FREECAD ASSEMBLY — COMPONENT RECIPES ("#110-000 Assembly3")

This assembly document has 90 components, labeled P0..P89 below (a component is one placed body or linked part). 0 of them carry a construction recipe — the FreeCAD feature program that regenerates the part from scratch, quoted from this document or its linked companion documents; the rest are supplied as boundary geometry only. No exploded tour is included for this assembly.
COMPONENT P0 — geometry summary ("XR5_R_CC25_P10.16_H_5DD3C33E001"; no construction recipe available for this part):
  bounding box: 10.7 x 5.1 x 2.5 mm
  tessellated surface: 5,540 triangles
  volume: 34 mm^3 (25% of its bounding box)
  symmetry: 2-fold rotationally symmetric about the z axis; mirror-symmetric across its x mid-plane, y mid-plane
COMPONENT P1 — geometry summary ("RV55_Alpha_RV16AF-41-15R-XXX_5DD3C758"; no construction recipe available for this part):
  bounding box: 30.7 x 24.7 x 17.0 mm
  tessellated surface: 23,788 triangles
  volume: 1291 mm^3 (10% of its bounding box)
COMPONENT P2 — geometry summary ("JP20_R_0R_Wire_Jumper_P10.16_5DC277DA001"; no construction recipe available for this part):
  bounding box: 10.7 x 3.6 x 0.6 mm
  tessellated surface: 2,588 triangles
  volume: 4 mm^3 (18% of its bounding box)
  symmetry: 2-fold rotationally symmetric about the z axis; mirror-symmetric across its x mid-plane, y mid-plane
COMPONENT P3 — geometry summary ("JP20_R_0R_Wire_Jumper_P10.16_5DC277DA002"; no construction recipe available for this part):
  bounding box: 10.7 x 3.6 x 0.6 mm
  tessellated surface: 2,588 triangles
  volume: 4 mm^3 (18% of its bounding box)
  symmetry: 2-fold rotationally symmetric about the z axis; mirror-symmetric across its x mid-plane, y mid-plane
COMPONENT P4 — geometry summary ("JP20_R_0R_Wire_Jumper_P10.16_5DC277DA003"; no construction recipe available for this part):
  bounding box: 10.7 x 3.6 x 0.6 mm
  tessellated surface: 2,588 triangles
  volume: 4 mm^3 (18% of its bounding box)
  symmetry: 2-fold rotationally symmetric about the z axis; mirror-symmetric across its x mid-plane, y mid-plane
COMPONENT P5 — geometry summary ("JP20_R_0R_Wire_Jumper_P10.16_5DC277DA004"; no construction recipe available for this part):
  bounding box: 10.7 x 3.6 x 0.6 mm
  tessellated surface: 2,588 triangles
  volume: 4 mm^3 (18% of its bounding box)
  symmetry: 2-fold rotationally symmetric about the z axis; mirror-symmetric across its x mid-plane, y mid-plane
COMPONENT P6 — geometry summary ("JP20_R_0R_Wire_Jumper_P10.16_5DC277DA005"; no construction recipe available for this part):
  bounding box: 10.7 x 3.6 x 0.6 mm
  tessellated surface: 2,588 triangles
  volume: 4 mm^3 (18% of its bounding box)
  symmetry: 2-fold rotationally symmetric about the z axis; mirror-symmetric across its x mid-plane, y mid-plane
COMPONENT P7 — geometry summary ("JP20_R_0R_Wire_Jumper_P10.16_5DC277DA006"; no construction recipe available for this part):
  bounding box: 10.7 x 3.6 x 0.6 mm
  tessellated surface: 2,588 triangles
  volume: 4 mm^3 (18% of its bounding box)
  symmetry: 2-fold rotationally symmetric about the z axis; mirror-symmetric across its x mid-plane, y mid-plane
COMPONENT P8 — geometry summary ("JP20_R_0R_Wire_Jumper_P10.16_5DC277DA007"; no construction recipe available for this part):
  bounding box: 10.7 x 3.6 x 0.6 mm
  tessellated surface: 2,588 triangles
  volume: 4 mm^3 (18% of its bounding box)
  symmetry: 2-fold rotationally symmetric about the z axis; mirror-symmetric across its x mid-plane, y mid-plane
COMPONENT P9 — geometry summary ("JP20_R_0R_Wire_Jumper_P10.16_5DC277DA008"; no construction recipe available for this part):
  bounding box: 10.7 x 3.6 x 0.6 mm
  tessellated surface: 2,588 triangles
  volume: 4 mm^3 (18% of its bounding box)
  symmetry: 2-fold rotationally symmetric about the z axis; mirror-symmetric across its x mid-plane, y mid-plane
COMPONENT P10 — geometry summary ("JP20_R_0R_Wire_Jumper_P10.16_5DC277DA009"; no construction recipe available for this part):
  bounding box: 10.7 x 3.6 x 0.6 mm
  tessellated surface: 2,588 triangles
  volume: 4 mm^3 (18% of its bounding box)
  symmetry: 2-fold rotationally symmetric about the z axis; mirror-symmetric across its x mid-plane, y mid-plane
COMPONENT P11 — geometry summary ("JP20_R_0R_Wire_Jumper_P10.16_5DC277DA010"; no construction recipe available for this part):
  bounding box: 10.7 x 3.6 x 0.6 mm
  tessellated surface: 2,588 triangles
  volume: 4 mm^3 (18% of its bounding box)
  symmetry: 2-fold rotationally symmetric about the z axis; mirror-symmetric across its x mid-plane, y mid-plane
COMPONENT P12 — geometry summary ("JP20_R_0R_Wire_Jumper_P10.16_5DC277DA011"; no construction recipe available for this part):
  bounding box: 10.7 x 3.6 x 0.6 mm
  tessellated surface: 2,588 triangles
  volume: 4 mm^3 (18% of its bounding box)
  symmetry: 2-fold rotationally symmetric about the z axis; mirror-symmetric across its x mid-plane, y mid-plane
COMPONENT P13 — geometry summary ("JP20_R_0R_Wire_Jumper_P10.16_5DC277DA012"; no construction recipe available for this part):
  bounding box: 10.7 x 3.6 x 0.6 mm
  tessellated surface: 2,588 triangles
  volume: 4 mm^3 (18% of its bounding box)
  symmetry: 2-fold rotationally symmetric about the z axis; mirror-symmetric across its x mid-plane, y mid-plane
COMPONENT P14 — geometry summary ("JP20_R_0R_Wire_Jumper_P10.16_5DC277DA013"; no construction recipe available for this part):
  bounding box: 10.7 x 3.6 x 0.6 mm
  tessellated surface: 2,588 triangles
  volume: 4 mm^3 (18% of its bounding box)
  symmetry: 2-fold rotationally symmetric about the z axis; mirror-symmetric across its x mid-plane, y mid-plane
COMPONENT P15 — geometry summary ("JP20_R_0R_Wire_Jumper_P10.16_5DC277DA014"; no construction recipe available for this part):
  bounding box: 10.7 x 3.6 x 0.6 mm
  tessellated surface: 2,588 triangles
  volume: 4 mm^3 (18% of its bounding box)
  symmetry: 2-fold rotationally symmetric about the z axis; mirror-symmetric across its x mid-plane, y mid-plane
COMPONENT P16 — geometry summary ("XC10_Nichicon_UMA_Straight_D5_H5_P2_d0.45_LL2.6_5DC00C0A001"; no construction recipe available for this part):
  bounding box: 7.6 x 5.0 x 5.0 mm
  tessellated surface: 17,406 triangles
  volume: 97 mm^3 (51% of its bounding box)
  symmetry: 2-fold rotationally symmetric about the z axis; mirror-symmetric across its x mid-plane, y mid-plane
COMPONENT P17 — geometry summary ("XC12_Nichicon_UMA_Straight_D8_H5_P2.5_d0.45_LL2.6_5DCF4B088"; no construction recipe available for this part):
  bounding box: 8.0 x 8.0 x 7.6 mm
  tessellated surface: 17,380 triangles
  volume: 248 mm^3 (51% of its bounding box)
  symmetry: 2-fold rotationally symmetric about the z axis; mirror-symmetric across its x mid-plane, y mid-plane
COMPONENT P18 — geometry summary ("XC10_Nichicon_UMA_Straight_D5_H5_P2_d0.45_LL2.6_5DC00C0A002"; no construction recipe available for this part):
  bounding box: 7.6 x 5.0 x 5.0 mm
  tessellated surface: 17,406 triangles
  volume: 97 mm^3 (51% of its bounding box)
  symmetry: 2-fold rotationally symmetric about the z axis; mirror-symmetric across its x mid-plane, y mid-plane
COMPONENT P19 — geometry summary ("XD6_DO-41_P10.16_5DC00C073"; no construction recipe available for this part):
  bounding box: 10.9 x 5.0 x 2.4 mm
  tessellated surface: 7,540 triangles
  volume: 26 mm^3 (20% of its bounding box)
  symmetry: 2-fold rotationally symmetric about the z axis
COMPONENT P20 — geometry summary ("XD6_DO-41_P10.16_5DC00C074"; no construction recipe available for this part):
  bounding box: 10.9 x 5.0 x 2.4 mm
  tessellated surface: 7,540 triangles
  volume: 26 mm^3 (20% of its bounding box)
  symmetry: 2-fold rotationally symmetric about the z axis
COMPONENT P21 — geometry summary ("XR5_R_CC25_P10.16_H_5DD3C33E002"; no construction recipe available for this part):
  bounding box: 10.7 x 5.1 x 2.5 mm
  tessellated surface: 5,540 triangles
  volume: 34 mm^3 (25% of its bounding box)
  symmetry: 2-fold rotationally symmetric about the z axis; mirror-symmetric across its x mid-plane, y mid-plane
COMPONENT P22 — geometry summary ("XR5_R_CC25_P10.16_H_5DD3C33E003"; no construction recipe available for this part):
  bounding box: 10.7 x 5.1 x 2.5 mm
  tessellated surface: 5,540 triangles
  volume: 34 mm^3 (25% of its bounding box)
  symmetry: 2-fold rotationally symmetric about the z axis; mirror-symmetric across its x mid-plane, y mid-plane
COMPONENT P23 — geometry summary ("XR5_R_CC25_P10.16_H_5DD3C33E004"; no construction recipe available for this part):
  bounding box: 10.7 x 5.1 x 2.5 mm
  tessellated surface: 5,540 triangles
  volume: 34 mm^3 (25% of its bounding box)
  symmetry: 2-fold rotationally symmetric about the z axis; mirror-symmetric across its x mid-plane, y mid-plane
COMPONENT P24 — geometry summary ("XR5_R_CC25_P10.16_H_5DD3C33E005"; no construction recipe available for this part):
  bounding box: 10.7 x 5.1 x 2.5 mm
  tessellated surface: 5,540 triangles
  volume: 34 mm^3 (25% of its bounding box)
  symmetry: 2-fold rotationally symmetric about the z axis; mirror-symmetric across its x mid-plane, y mid-plane
COMPONENT P25 — geometry summary ("XR5_R_CC25_P10.16_H_5DD3C33E006"; no construction recipe available for this part):
  bounding box: 10.7 x 5.1 x 2.5 mm
  tessellated surface: 5,540 triangles
  volume: 34 mm^3 (25% of its bounding box)
  symmetry: 2-fold rotationally symmetric about the z axis; mirror-symmetric across its x mid-plane, y mid-plane
COMPONENT P26 — geometry summary ("XR5_R_CC25_P10.16_H_5DD3C33E007"; no construction recipe available for this part):
  bounding box: 10.7 x 5.1 x 2.5 mm
  tessellated surface: 5,540 triangles
  volume: 34 mm^3 (25% of its bounding box)
  symmetry: 2-fold rotationally symmetric about the z axis; mirror-symmetric across its x mid-plane, y mid-plane
COMPONENT P27 — geometry summary ("XR5_R_CC25_P10.16_H_5DD3C33E008"; no construction recipe available for this part):
  bounding box: 10.7 x 5.1 x 2.5 mm
  tessellated surface: 5,540 triangles
  volume: 34 mm^3 (25% of its bounding box)
  symmetry: 2-fold rotationally symmetric about the z axis; mirror-symmetric across its x mid-plane, y mid-plane
COMPONENT P28 — geometry summary ("XR5_R_CC25_P10.16_H_5DD3C33E009"; no construction recipe available for this part):
  bounding box: 10.7 x 5.1 x 2.5 mm
  tessellated surface: 5,540 triangles
  volume: 34 mm^3 (25% of its bounding box)
  symmetry: 2-fold rotationally symmetric about the z axis; mirror-symmetric across its x mid-plane, y mid-plane
COMPONENT P29 — geometry summary ("XR5_R_CC25_P10.16_H_5DD3C33E010"; no construction recipe available for this part):
  bounding box: 10.7 x 5.1 x 2.5 mm
  tessellated surface: 5,540 triangles
  volume: 34 mm^3 (25% of its bounding box)
  symmetry: 2-fold rotationally symmetric about the z axis; mirror-symmetric across its x mid-plane, y mid-plane
COMPONENT P30 — geometry summary ("XR5_R_CC25_P10.16_H_5DD3C33E011"; no construction recipe available for this part):
  bounding box: 10.7 x 5.1 x 2.5 mm
  tessellated surface: 5,540 triangles
  volume: 34 mm^3 (25% of its bounding box)
  symmetry: 2-fold rotationally symmetric about the z axis; mirror-symmetric across its x mid-plane, y mid-plane
COMPONENT P31 — geometry summary ("XR5_R_CC25_P10.16_H_5DD3C33E012"; no construction recipe available for this part):
  bounding box: 10.7 x 5.1 x 2.5 mm
  tessellated surface: 5,540 triangles
  volume: 34 mm^3 (25% of its bounding box)
  symmetry: 2-fold rotationally symmetric about the z axis; mirror-symmetric across its x mid-plane, y mid-plane
COMPONENT P32 — geometry summary ("XR5_R_CC25_P10.16_H_5DD3C33E013"; no construction recipe available for this part):
  bounding box: 10.7 x 5.1 x 2.5 mm
  tessellated surface: 5,540 triangles
  volume: 34 mm^3 (25% of its bounding box)
  symmetry: 2-fold rotationally symmetric about the z axis; mirror-symmetric across its x mid-plane, y mid-plane
COMPONENT P33 — geometry summary ("XR5_R_CC25_P10.16_H_5DD3C33E014"; no construction recipe available for this part):
  bounding box: 10.7 x 5.1 x 2.5 mm
  tessellated surface: 5,540 triangles
  volume: 34 mm^3 (25% of its bounding box)
  symmetry: 2-fold rotationally symmetric about the z axis; mirror-symmetric across its x mid-plane, y mid-plane
COMPONENT P34 — geometry summary ("XR5_R_CC25_P10.16_H_5DD3C33E015"; no construction recipe available for this part):
  bounding box: 10.7 x 5.1 x 2.5 mm
  tessellated surface: 5,540 triangles
  volume: 34 mm^3 (25% of its bounding box)
  symmetry: 2-fold rotationally symmetric about the z axis; mirror-symmetric across its x mid-plane, y mid-plane
COMPONENT P35 — geometry summary ("XR5_R_CC25_P10.16_H_5DD3C33E016"; no construction recipe available for this part):
  bounding box: 10.7 x 5.1 x 2.5 mm
  tessellated surface: 5,540 triangles
  volume: 34 mm^3 (25% of its bounding box)
  symmetry: 2-fold rotationally symmetric about the z axis; mirror-symmetric across its x mid-plane, y mid-plane
COMPONENT P36 — geometry summary ("XR5_R_CC25_P10.16_H_5DD3C33E017"; no construction recipe available for this part):
  bounding box: 10.7 x 5.1 x 2.5 mm
  tessellated surface: 5,540 triangles
  volume: 34 mm^3 (25% of its bounding box)
  symmetry: 2-fold rotationally symmetric about the z axis; mirror-symmetric across its x mid-plane, y mid-plane
COMPONENT P37 — geometry summary ("XR5_R_CC25_P10.16_H_5DD3C33E018"; no construction recipe available for this part):
  bounding box: 10.7 x 5.1 x 2.5 mm
  tessellated surface: 5,540 triangles
  volume: 34 mm^3 (25% of its bounding box)
  symmetry: 2-fold rotationally symmetric about the z axis; mirror-symmetric across its x mid-plane, y mid-plane
COMPONENT P38 — geometry summary ("XR5_R_CC25_P10.16_H_5DD3C33E019"; no construction recipe available for this part):
  bounding box: 10.7 x 5.1 x 2.5 mm
  tessellated surface: 5,540 triangles
  volume: 34 mm^3 (25% of its bounding box)
  symmetry: 2-fold rotationally symmetric about the z axis; mirror-symmetric across its x mid-plane, y mid-plane
COMPONENT P39 — geometry summary ("XR5_R_CC25_P10.16_H_5DD3C33E020"; no construction recipe available for this part):
  bounding box: 10.7 x 5.1 x 2.5 mm
  tessellated surface: 5,540 triangles
  volume: 34 mm^3 (25% of its bounding box)
  symmetry: 2-fold rotationally symmetric about the z axis; mirror-symmetric across its x mid-plane, y mid-plane
COMPONENT P40 — geometry summary ("XR5_R_CC25_P10.16_H_5DD3C33E021"; no construction recipe available for this part):
  bounding box: 10.7 x 5.1 x 2.5 mm
  tessellated surface: 5,540 triangles
  volume: 34 mm^3 (25% of its bounding box)
  symmetry: 2-fold rotationally symmetric about the z axis; mirror-symmetric across its x mid-plane, y mid-plane
COMPONENT P41 — geometry summary ("XR5_R_CC25_P10.16_H_5DD3C33E022"; no construction recipe available for this part):
  bounding box: 10.7 x 5.1 x 2.5 mm
  tessellated surface: 5,540 triangles
  volume: 34 mm^3 (25% of its bounding box)
  symmetry: 2-fold rotationally symmetric about the z axis; mirror-symmetric across its x mid-plane, y mid-plane
COMPONENT P42 — geometry summary ("XR5_R_CC25_P10.16_H_5DD3C33E023"; no construction recipe available for this part):
  bounding box: 10.7 x 5.1 x 2.5 mm
  tessellated surface: 5,540 triangles
  volume: 34 mm^3 (25% of its bounding box)
  symmetry: 2-fold rotationally symmetric about the z axis; mirror-symmetric across its x mid-plane, y mid-plane
COMPONENT P43 — geometry summary ("XR5_R_CC25_P10.16_H_5DD3C33E024"; no construction recipe available for this part):
  bounding box: 10.7 x 5.1 x 2.5 mm
  tessellated surface: 5,540 triangles
  volume: 34 mm^3 (25% of its bounding box)
  symmetry: 2-fold rotationally symmetric about the z axis; mirror-symmetric across its x mid-plane, y mid-plane
COMPONENT P44 — geometry summary ("XR5_R_CC25_P10.16_H_5DD3C33E025"; no construction recipe available for this part):
  bounding box: 10.7 x 5.1 x 2.5 mm
  tessellated surface: 5,540 triangles
  volume: 34 mm^3 (25% of its bounding box)
  symmetry: 2-fold rotationally symmetric about the z axis; mirror-symmetric across its x mid-plane, y mid-plane
COMPONENT P45 — geometry summary ("XR5_R_CC25_P10.16_H_5DD3C33E026"; no construction recipe available for this part):
  bounding box: 10.7 x 5.1 x 2.5 mm
  tessellated surface: 5,540 triangles
  volume: 34 mm^3 (25% of its bounding box)
  symmetry: 2-fold rotationally symmetric about the z axis; mirror-symmetric across its x mid-plane, y mid-plane
COMPONENT P46 — geometry summary ("XR5_R_CC25_P10.16_H_5DD3C33E027"; no construction recipe available for this part):
  bounding box: 10.7 x 5.1 x 2.5 mm
  tessellated surface: 5,540 triangles
  volume: 34 mm^3 (25% of its bounding box)
  symmetry: 2-fold rotationally symmetric about the z axis; mirror-symmetric across its x mid-plane, y mid-plane
COMPONENT P47 — geometry summary ("XR5_R_CC25_P10.16_H_5DD3C33E028"; no construction recipe available for this part):
  bounding box: 10.7 x 5.1 x 2.5 mm
  tessellated surface: 5,540 triangles
  volume: 34 mm^3 (25% of its bounding box)
  symmetry: 2-fold rotationally symmetric about the z axis; mirror-symmetric across its x mid-plane, y mid-plane
COMPONENT P48 — geometry summary ("XR5_R_CC25_P10.16_H_5DD3C33E029"; no construction recipe available for this part):
  bounding box: 10.7 x 5.1 x 2.5 mm
  tessellated surface: 5,540 triangles
  volume: 34 mm^3 (25% of its bounding box)
  symmetry: 2-fold rotationally symmetric about the z axis; mirror-symmetric across its x mid-plane, y mid-plane
COMPONENT P49 — geometry summary ("XR5_R_CC25_P10.16_H_5DD3C33E030"; no construction recipe available for this part):
  bounding box: 10.7 x 5.1 x 2.5 mm
  tessellated surface: 5,540 triangles
  volume: 34 mm^3 (25% of its bounding box)
  symmetry: 2-fold rotationally symmetric about the z axis; mirror-symmetric across its x mid-plane, y mid-plane
COMPONENT P50 — geometry summary ("XR5_R_CC25_P10.16_H_5DD3C33E031"; no construction recipe available for this part):
  bounding box: 10.7 x 5.1 x 2.5 mm
  tessellated surface: 5,540 triangles
  volume: 34 mm^3 (25% of its bounding box)
  symmetry: 2-fold rotationally symmetric about the z axis; mirror-symmetric across its x mid-plane, y mid-plane
COMPONENT P51 — geometry summary ("XR5_R_CC25_P10.16_H_5DD3C33E032"; no construction recipe available for this part):
  bounding box: 10.7 x 5.1 x 2.5 mm
  tessellated surface: 5,540 triangles
  volume: 34 mm^3 (25% of its bounding box)
  symmetry: 2-fold rotationally symmetric about the z axis; mirror-symmetric across its x mid-plane, y mid-plane
COMPONENT P52 — geometry summary ("XR5_R_CC25_P10.16_H_5DD3C33E033"; no construction recipe available for this part):
  bounding box: 10.7 x 5.1 x 2.5 mm
  tessellated surface: 5,540 triangles
  volume: 34 mm^3 (25% of its bounding box)
  symmetry: 2-fold rotationally symmetric about the z axis; mirror-symmetric across its x mid-plane, y mid-plane
COMPONENT P53 — geometry summary ("XR5_R_CC25_P10.16_H_5DD3C33E034"; no construction recipe available for this part):
  bounding box: 10.7 x 5.1 x 2.5 mm
  tessellated surface: 5,540 triangles
  volume: 34 mm^3 (25% of its bounding box)
  symmetry: 2-fold rotationally symmetric about the z axis; mirror-symmetric across its x mid-plane, y mid-plane
COMPONENT P54 — geometry summary ("XR5_R_CC25_P10.16_H_5DD3C33E035"; no construction recipe available for this part):
  bounding box: 10.7 x 5.1 x 2.5 mm
  tessellated surface: 5,540 triangles
  volume: 34 mm^3 (25% of its bounding box)
  symmetry: 2-fold rotationally symmetric about the z axis; mirror-symmetric across its x mid-plane, y mid-plane
COMPONENT P55 — geometry summary ("XR5_R_CC25_P10.16_H_5DD3C33E036"; no construction recipe available for this part):
  bounding box: 10.7 x 5.1 x 2.5 mm
  tessellated surface: 5,540 triangles
  volume: 34 mm^3 (25% of its bounding box)
  symmetry: 2-fold rotationally symmetric about the z axis; mirror-symmetric across its x mid-plane, y mid-plane
COMPONENT P56 — geometry summary ("XR5_R_CC25_P10.16_H_5DD3C33E037"; no construction recipe available for this part):
  bounding box: 10.7 x 5.1 x 2.5 mm
  tessellated surface: 5,540 triangles
  volume: 34 mm^3 (25% of its bounding box)
  symmetry: 2-fold rotationally symmetric about the z axis; mirror-symmetric across its x mid-plane, y mid-plane
COMPONENT P57 — geometry summary ("XR5_R_CC25_P10.16_H_5DD3C33E038"; no construction recipe available for this part):
  bounding box: 10.7 x 5.1 x 2.5 mm
  tessellated surface: 5,540 triangles
  volume: 34 mm^3 (25% of its bounding box)
  symmetry: 2-fold rotationally symmetric about the z axis; mirror-symmetric across its x mid-plane, y mid-plane
COMPONENT P58 — geometry summary ("XR5_R_CC25_P10.16_H_5DD3C33E039"; no construction recipe available for this part):
  bounding box: 10.7 x 5.1 x 2.5 mm
  tessellated surface: 5,540 triangles
  volume: 34 mm^3 (25% of its bounding box)
  symmetry: 2-fold rotationally symmetric about the z axis; mirror-symmetric across its x mid-plane, y mid-plane
COMPONENT P59 — geometry summary ("XR5_R_CC25_P10.16_H_5DD3C33E040"; no construction recipe available for this part):
  bounding box: 10.7 x 5.1 x 2.5 mm
  tessellated surface: 5,540 triangles
  volume: 34 mm^3 (25% of its bounding box)
  symmetry: 2-fold rotationally symmetric about the z axis; mirror-symmetric across its x mid-plane, y mid-plane
COMPONENT P60 — geometry summary ("XR5_R_CC25_P10.16_H_5DD3C33E041"; no construction recipe available for this part):
  bounding box: 10.7 x 5.1 x 2.5 mm
  tessellated surface: 5,540 triangles
  volume: 34 mm^3 (25% of its bounding box)
  symmetry: 2-fold rotationally symmetric about the z axis; mirror-symmetric across its x mid-plane, y mid-plane
COMPONENT P61 — geometry summary ("XR5_R_CC25_P10.16_H_5DD3C33E042"; no construction recipe available for this part):
  bounding box: 10.7 x 5.1 x 2.5 mm
  tessellated surface: 5,540 triangles
  volume: 34 mm^3 (25% of its bounding box)
  symmetry: 2-fold rotationally symmetric about the z axis; mirror-symmetric across its x mid-plane, y mid-plane
COMPONENT P62 — geometry summary ("XR5_R_CC25_P10.16_H_5DD3C33E043"; no construction recipe available for this part):
  bounding box: 10.7 x 5.1 x 2.5 mm
  tessellated surface: 5,540 triangles
  volume: 34 mm^3 (25% of its bounding box)
  symmetry: 2-fold rotationally symmetric about the z axis; mirror-symmetric across its x mid-plane, y mid-plane
COMPONENT P63 — geometry summary ("XR5_R_CC25_P10.16_H_5DD3C33E044"; no construction recipe available for this part):
  bounding box: 10.7 x 5.1 x 2.5 mm
  tessellated surface: 5,540 triangles
  volume: 34 mm^3 (25% of its bounding box)
  symmetry: 2-fold rotationally symmetric about the z axis; mirror-symmetric across its x mid-plane, y mid-plane
COMPONENT P64 — geometry summary ("XR5_R_CC25_P10.16_H_5DD3C33E045"; no construction recipe available for this part):
  bounding box: 10.7 x 5.1 x 2.5 mm
  tessellated surface: 5,540 triangles
  volume: 34 mm^3 (25% of its bounding box)
  symmetry: 2-fold rotationally symmetric about the z axis; mirror-symmetric across its x mid-plane, y mid-plane
COMPONENT P65 — geometry summary ("XR5_R_CC25_P10.16_H_5DD3C33E046"; no construction recipe available for this part):
  bounding box: 10.7 x 5.1 x 2.5 mm
  tessellated surface: 5,540 triangles
  volume: 34 mm^3 (25% of its bounding box)
  symmetry: 2-fold rotationally symmetric about the z axis; mirror-symmetric across its x mid-plane, y mid-plane
COMPONENT P66 — geometry summary ("XR5_R_CC25_P10.16_H_5DD3C33E047"; no construction recipe available for this part):
  bounding box: 10.7 x 5.1 x 2.5 mm
  tessellated surface: 5,540 triangles
  volume: 34 mm^3 (25% of its bounding box)
  symmetry: 2-fold rotationally symmetric about the z axis; mirror-symmetric across its x mid-plane, y mid-plane
COMPONENT P67 — geometry summary ("XR5_R_CC25_P10.16_H_5DD3C33E048"; no construction recipe available for this part):
  bounding box: 10.7 x 5.1 x 2.5 mm
  tessellated surface: 5,540 triangles
  volume: 34 mm^3 (25% of its bounding box)
  symmetry: 2-fold rotationally symmetric about the z axis; mirror-symmetric across its x mid-plane, y mid-plane
COMPONENT P68 — geometry summary ("XR5_R_CC25_P10.16_H_5DD3C33E049"; no construction recipe available for this part):
  bounding box: 10.7 x 5.1 x 2.5 mm
  tessellated surface: 5,540 triangles
  volume: 34 mm^3 (25% of its bounding box)
  symmetry: 2-fold rotationally symmetric about the z axis; mirror-symmetric across its x mid-plane, y mid-plane
COMPONENT P69 — geometry summary ("XR5_R_CC25_P10.16_H_5DD3C33E050"; no construction recipe available for this part):
  bounding box: 10.7 x 5.1 x 2.5 mm
  tessellated surface: 5,540 triangles
  volume: 34 mm^3 (25% of its bounding box)
  symmetry: 2-fold rotationally symmetric about the z axis; mirror-symmetric across its x mid-plane, y mid-plane
COMPONENT P70 — geometry summary ("XD6_DO-41_P10.16_5DC00C075"; no construction recipe available for this part):
  bounding box: 10.9 x 5.0 x 2.4 mm
  tessellated surface: 7,540 triangles
  volume: 26 mm^3 (20% of its bounding box)
  symmetry: 2-fold rotationally symmetric about the z axis
COMPONENT P71 — geometry summary ("XD6_DO-41_P10.16_5DC00C076"; no construction recipe available for this part):
  bounding box: 10.9 x 5.0 x 2.4 mm
  tessellated surface: 7,540 triangles
  volume: 26 mm^3 (20% of its bounding box)
  symmetry: 2-fold rotationally symmetric about the z axis
COMPONENT P72 — geometry summary ("XD6_DO-41_P10.16_5DC00C077"; no construction recipe available for this part):
  bounding box: 10.9 x 5.0 x 2.4 mm
  tessellated surface: 7,540 triangles
  volume: 26 mm^3 (20% of its bounding box)
  symmetry: 2-fold rotationally symmetric about the z axis
COMPONENT P73 — geometry summary ("XD6_DO-41_P10.16_5DC00C078"; no construction recipe available for this part):
  bounding box: 10.9 x 5.0 x 2.4 mm
  tessellated surface: 7,540 triangles
  volume: 26 mm^3 (20% of its bounding box)
  symmetry: 2-fold rotationally symmetric about the z axis
COMPONENT P74 — geometry summary ("XD6_DO-41_P10.16_5DC00C079"; no construction recipe available for this part):
  bounding box: 10.9 x 5.0 x 2.4 mm
  tessellated surface: 7,540 triangles
  volume: 26 mm^3 (20% of its bounding box)
  symmetry: 2-fold rotationally symmetric about the z axis
COMPONENT P75 — geometry summary ("XD6_DO-41_P10.16_5DC00C080"; no construction recipe available for this part):
  bounding box: 10.9 x 5.0 x 2.4 mm
  tessellated surface: 7,540 triangles
  volume: 26 mm^3 (20% of its bounding box)
  symmetry: 2-fold rotationally symmetric about the z axis
COMPONENT P76 — geometry summary ("XD6_DO-41_P10.16_5DC00C081"; no construction recipe available for this part):
  bounding box: 10.9 x 5.0 x 2.4 mm
  tessellated surface: 7,540 triangles
  volume: 26 mm^3 (20% of its bounding box)
  symmetry: 2-fold rotationally symmetric about the z axis
COMPONENT P77 — geometry summary ("XD6_DO-41_P10.16_5DC00C082"; no construction recipe available for this part):
  bounding box: 10.9 x 5.0 x 2.4 mm
  tessellated surface: 7,540 triangles
  volume: 26 mm^3 (20% of its bounding box)
  symmetry: 2-fold rotationally symmetric about the z axis
COMPONENT P78 — geometry summary ("XD6_DO-41_P10.16_5DC00C083"; no construction recipe available for this part):
  bounding box: 10.9 x 5.0 x 2.4 mm
  tessellated surface: 7,540 triangles
  volume: 26 mm^3 (20% of its bounding box)
  symmetry: 2-fold rotationally symmetric about the z axis
COMPONENT P79 — geometry summary ("XU1_RC4558P_5DC00D2F001"; no construction recipe available for this part):
  bounding box: 9.6 x 7.9 x 7.1 mm
  tessellated surface: 2,594 triangles
  volume: 205 mm^3 (38% of its bounding box)
  symmetry: mirror-symmetric across its y mid-plane
COMPONENT P80 — geometry summary ("XU1_RC4558P_5DC00D2F002"; no construction recipe available for this part):
  bounding box: 9.6 x 7.9 x 7.1 mm
  tessellated surface: 2,594 triangles
  volume: 205 mm^3 (38% of its bounding box)
  symmetry: mirror-symmetric across its y mid-plane
COMPONENT P81 — geometry summary ("XU1_RC4558P_5DC00D2F003"; no construction recipe available for this part):
  bounding box: 9.6 x 7.9 x 7.1 mm
  tessellated surface: 2,594 triangles
  volume: 205 mm^3 (38% of its bounding box)
  symmetry: mirror-symmetric across its y mid-plane
COMPONENT P82 — geometry summary ("XU1_RC4558P_5DC00D2F004"; no construction recipe available for this part):
  bounding box: 9.6 x 7.9 x 7.1 mm
  tessellated surface: 2,594 triangles
  volume: 205 mm^3 (38% of its bounding box)
  symmetry: mirror-symmetric across its y mid-plane
COMPONENT P83 — geometry summary ("XU1_RC4558P_5DC00D2F005"; no construction recipe available for this part):
  bounding box: 9.6 x 7.9 x 7.1 mm
  tessellated surface: 2,594 triangles
  volume: 205 mm^3 (38% of its bounding box)
  symmetry: mirror-symmetric across its y mid-plane
COMPONENT P84 — geometry summary ("XQ2_2N3904TAR_5DC00CE006"; no construction recipe available for this part):
  bounding box: 10.4 x 5.5 x 3.6 mm
  tessellated surface: 1,644 triangles
  volume: 74 mm^3 (35% of its bounding box)
  symmetry: mirror-symmetric across its x mid-plane
COMPONENT P85 — geometry summary ("C23_FKS2G016801B00KSSD_5DD3B7C003"; no construction recipe available for this part):
  bounding box: 9.5 x 7.2 x 3.1 mm
  tessellated surface: 4,768 triangles
  volume: 140 mm^3 (67% of its bounding box)
  symmetry: 2-fold rotationally symmetric about the z axis
COMPONENT P86 — geometry summary ("C23_FKS2G016801B00KSSD_5DD3B7C004"; no construction recipe available for this part):
  bounding box: 9.5 x 7.2 x 3.1 mm
  tessellated surface: 4,768 triangles
  volume: 140 mm^3 (67% of its bounding box)
  symmetry: 2-fold rotationally symmetric about the z axis
COMPONENT P87 — geometry summary ("C23_FKS2G016801B00KSSD_5DD3B7C005"; no construction recipe available for this part):
  bounding box: 9.5 x 7.2 x 3.1 mm
  tessellated surface: 4,768 triangles
  volume: 140 mm^3 (67% of its bounding box)
  symmetry: 2-fold rotationally symmetric about the z axis
COMPONENT P88 — geometry summary ("C23_FKS2G016801B00KSSD_5DD3B7C006"; no construction recipe available for this part):
  bounding box: 9.5 x 7.2 x 3.1 mm
  tessellated surface: 4,768 triangles
  volume: 140 mm^3 (67% of its bounding box)
  symmetry: 2-fold rotationally symmetric about the z axis
COMPONENT P89 — geometry summary ("C23_FKS2G016801B00KSSD_5DD3B7C007"; no construction recipe available for this part):
  bounding box: 9.5 x 7.2 x 3.1 mm
  tessellated surface: 4,768 triangles
  volume: 140 mm^3 (67% of its bounding box)
  symmetry: 2-fold rotationally symmetric about the z axis
PROVENANCE & LICENSES
A FreeCAD (.FCStd) document from a public repository crawl; recipes are the document's own serialized feature recipes (and, for linked parts, companion documents' recipes).
License: as declared in the source repository (recorded in the dataset sidecar).
